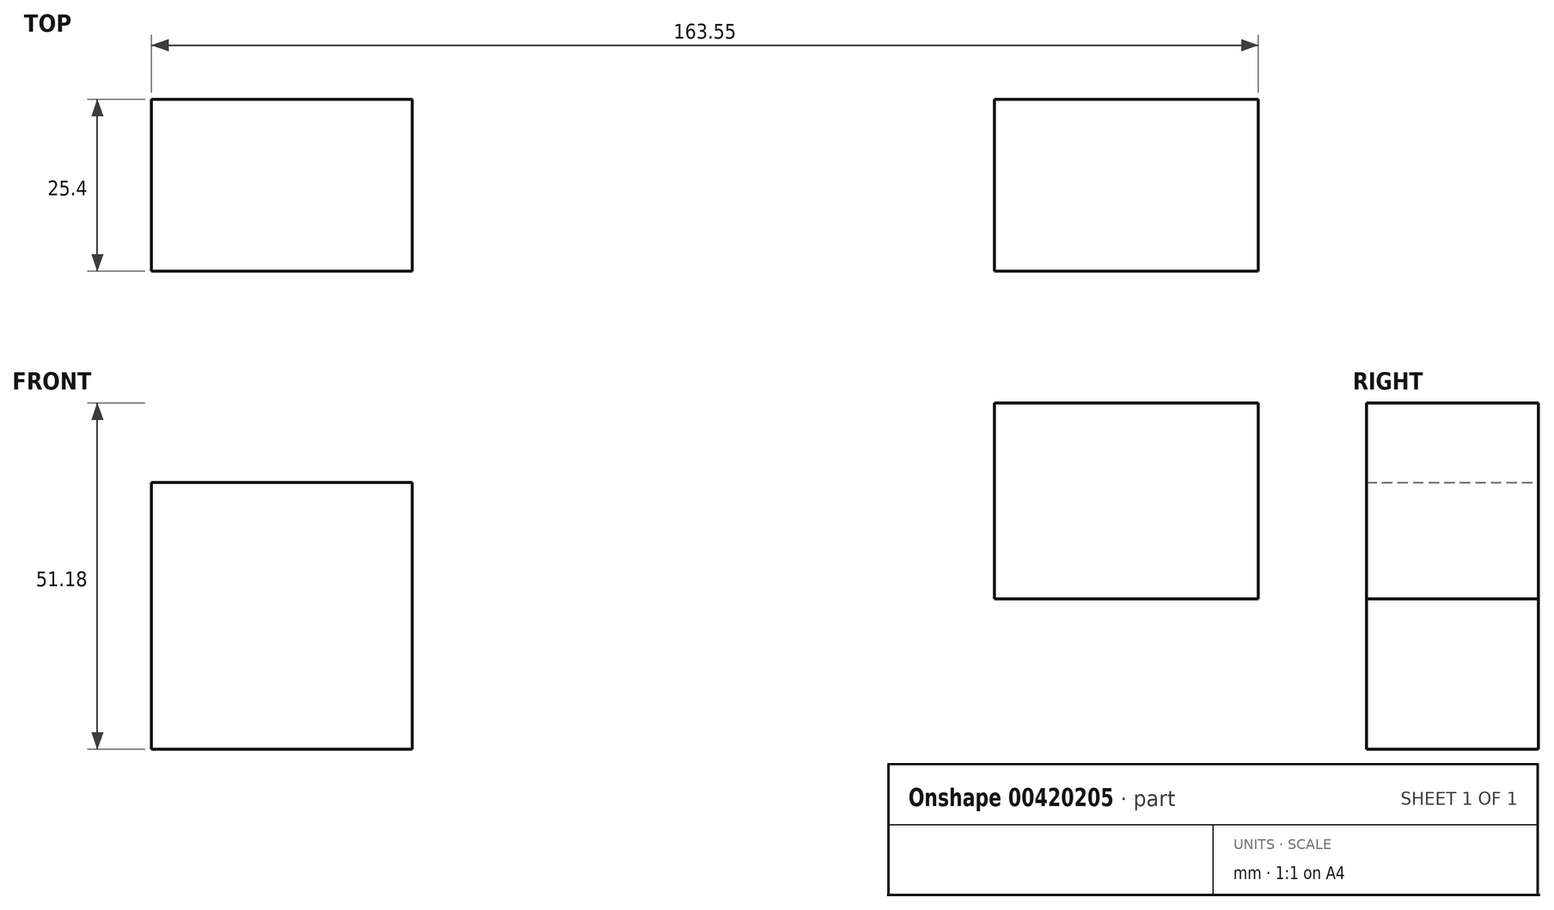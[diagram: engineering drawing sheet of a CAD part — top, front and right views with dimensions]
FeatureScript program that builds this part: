
annotation { "Feature Type Name" : "Feature", "Feature Type Description" : "" }
export const myFeature = defineFeature(function(context is Context, id is Id, definition is map)
    precondition{}
    {
        {
            var Q0;
            Q0=qCreatedBy(makeId("Front.planeOp"),FACE);
            var sketch = newSketch(context, id + "F0", { "sketchPlane" : qUnion([Q0])});
            skLineSegment(sketch, "E0.bottom", {"start": v(-59.36, 45.54) * mm, "end": v(-97.9, 45.54) * mm});
            skLineSegment(sketch, "E0.top", {"start": v(-59.36, 6.08) * mm, "end": v(-97.9, 6.08) * mm});
            skLineSegment(sketch, "E0.left", {"start": v(-59.36, 45.54) * mm, "end": v(-59.36, 6.08) * mm});
            skLineSegment(sketch, "E0.right", {"start": v(-97.9, 45.54) * mm, "end": v(-97.9, 6.08) * mm});
            skSolve(sketch);
        }
        {
            var Q0;
            Q0 = qSketchRegion(id + "F0", true);
            extrude(context, id + "F1", {"entities" : qUnion([Q0]), "depth" : 25.4 * mm});
        }
        {
            var Q0;
            Q0=qCreatedBy(makeId("Front.planeOp"),FACE);
            var sketch = newSketch(context, id + "F2", { "sketchPlane" : qUnion([Q0])});
            skLineSegment(sketch, "E1.bottom", {"start": v(26.64, 57.26) * mm, "end": v(65.66, 57.26) * mm});
            skLineSegment(sketch, "E1.top", {"start": v(26.64, 28.32) * mm, "end": v(65.66, 28.32) * mm});
            skLineSegment(sketch, "E1.left", {"start": v(26.64, 57.26) * mm, "end": v(26.64, 28.32) * mm});
            skLineSegment(sketch, "E1.right", {"start": v(65.66, 57.26) * mm, "end": v(65.66, 28.32) * mm});
            skSolve(sketch);
        }
        {
            var Q0;
            Q0=makeQuery(id+"F2.imprint","IMPRINT",FACE,{"disambiguationData":[TD([[makeQuery(id+"F2.imprint","IMPRINT",EDGE,{"derivedFrom":sQuery(id+"F2.wireOp",EDGE,"E1.bottom")}),-1.0]])]});
            extrude(context, id + "F3", {"entities" : qUnion([Q0]), "depth" : 25.4 * mm});
        }
    });
